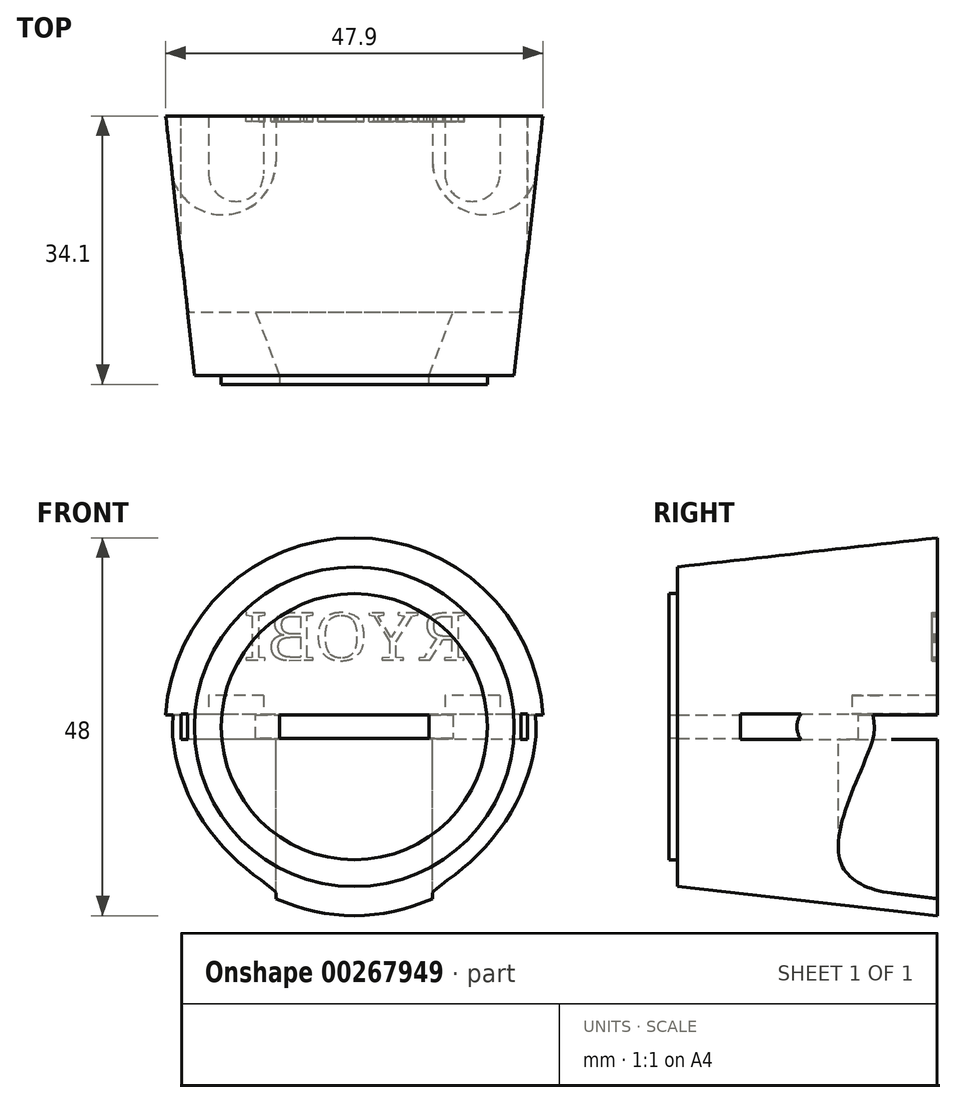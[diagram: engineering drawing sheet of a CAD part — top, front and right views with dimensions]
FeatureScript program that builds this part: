
annotation { "Feature Type Name" : "Feature", "Feature Type Description" : "" }
export const myFeature = defineFeature(function(context is Context, id is Id, definition is map)
    precondition{}
    {
        {
            var Q0;
            Q0=qCreatedBy(makeId("Top.planeOp"),FACE);
            var sketch = newSketch(context, id + "F0", { "sketchPlane" : qUnion([Q0])});
            skLineSegment(sketch, "E0", {"start": v(-68.5, 0) * mm, "end": v(-16.9, 0) * mm, "construction": true});
            skLineSegment(sketch, "E1", {"start": v(0, 74.1) * mm, "end": v(0, -57) * mm, "construction": true});
            skLineSegment(sketch, "E2", {"start": v(-16.9, 0) * mm, "end": v(-20.3, 0) * mm});
            skLineSegment(sketch, "E3", {"start": v(-20.3, 0) * mm, "end": v(-24, 33) * mm});
            skLineSegment(sketch, "E4", {"start": v(-24, 33) * mm, "end": v(0, 33) * mm});
            skLineSegment(sketch, "E5", {"start": v(0, 33) * mm, "end": v(0, 0) * mm});
            skLineSegment(sketch, "E6", {"start": v(-16.9, 0) * mm, "end": v(-16.9, -1.1) * mm});
            skLineSegment(sketch, "E7", {"start": v(-16.9, -1.1) * mm, "end": v(0, -1.1) * mm});
            skLineSegment(sketch, "E8.trimOffspring", {"start": v(0, 0) * mm, "end": v(74.38, 0) * mm, "construction": true});
            skLineSegment(sketch, "E9", {"start": v(0, -1.1) * mm, "end": v(0, 0) * mm});
            skSolve(sketch);
        }
        {
            var Q0;
            Q0=makeQuery(id+"F0.imprint","IMPRINT",FACE,{"disambiguationData":[TD([[makeQuery(id+"F0.imprint","IMPRINT",EDGE,{"derivedFrom":sQuery(id+"F0.wireOp",EDGE,"E2")}),-1.0]])]});
            var Q1;
            Q1=sQuery(id+"F0.wireOp",EDGE,"E1");
            revolve(context, id + "F1", {"entities" : qUnion([Q0]), "axis" : qUnion([Q1]), "revolveType" : RevolveType.FULL});
        }
        {
            var Q0;
            Q0=makeQuery(id+"F1.opRevolve","SWEPT_FACE",FACE,{"disambiguationData":[OSD([sQuery(id+"F0.wireOp",EDGE,"E4")])]});
            var sketch = newSketch(context, id + "F2", { "sketchPlane" : qUnion([Q0])});
            skLineSegment(sketch, "E10", {"start": v(-37.33, 0) * mm, "end": v(38.29, 0) * mm, "construction": true});
            skLineSegment(sketch, "E11", {"start": v(0, 36.13) * mm, "end": v(0, -36.43) * mm, "construction": true});
            skLineSegment(sketch, "E12", {"start": v(-22, 0) * mm, "end": v(-22, 1.6) * mm});
            skLineSegment(sketch, "E13", {"start": v(-22, 1.6) * mm, "end": v(0, 1.6) * mm});
            skLineSegment(sketch, "E14.MirrorCS", {"start": v(-22, -1.6) * mm, "end": v(0, -1.6) * mm});
            skLineSegment(sketch, "E15.MirrorCS", {"start": v(-22, 0) * mm, "end": v(-22, -1.6) * mm});
            skLineSegment(sketch, "E16.MirrorCS", {"start": v(22, 1.6) * mm, "end": v(0, 1.6) * mm});
            skLineSegment(sketch, "E17.MirrorCS", {"start": v(22, -1.6) * mm, "end": v(0, -1.6) * mm});
            skLineSegment(sketch, "E18.MirrorCS", {"start": v(22, 0) * mm, "end": v(22, 1.6) * mm});
            skLineSegment(sketch, "E19.MirrorCS", {"start": v(22, 0) * mm, "end": v(22, -1.6) * mm});
            skSolve(sketch);
        }
        {
            var Q0;
            Q0=qCreatedBy(makeId("Top.planeOp"),FACE);
            var sketch = newSketch(context, id + "F3", { "sketchPlane" : qUnion([Q0])});
            skLineSegment(sketch, "E20", {"start": v(22, 33.22) * mm, "end": v(-22, 33.22) * mm});
            skLineSegment(sketch, "E21", {"start": v(-22, 33.22) * mm, "end": v(-9.5, 0) * mm});
            skLineSegment(sketch, "E22", {"start": v(9.5, 0) * mm, "end": v(22, 33.22) * mm});
            skLineSegment(sketch, "E23", {"start": v(-9.5, 0) * mm, "end": v(-9.5, -1.28) * mm});
            skLineSegment(sketch, "E24", {"start": v(9.5, -1.28) * mm, "end": v(9.5, 0) * mm});
            skLineSegment(sketch, "E25", {"start": v(-9.5, -1.28) * mm, "end": v(9.5, -1.28) * mm});
            skLineSegment(sketch, "E26", {"start": v(-23.43, 20.06) * mm, "end": v(-23.43, 27.36) * mm, "construction": true});
            skLineSegment(sketch, "E27", {"start": v(23.97, 20.01) * mm, "end": v(23.97, 26.32) * mm, "construction": true});
            skLineSegment(sketch, "E28", {"start": v(-32.98, 14.8) * mm, "end": v(30.34, 14.8) * mm, "construction": true});
            skSolve(sketch);
        }
        {
            var Q0;
            Q0 = qSketchRegion(id + "F3", true);
            extrude(context, id + "F4", {"entities" : qUnion([Q0]), "operationType" : NewBodyOperationType.REMOVE, "endBound" : BoundingType.SYMMETRIC, "depth" : 3 * mm, "offsetDistance" : 25 * mm});
        }
        {
            var Q0;
            Q0=qCreatedBy(makeId("Top.planeOp"),FACE);
            var sketch = newSketch(context, id + "F5", { "sketchPlane" : qUnion([Q0])});
            skLineSegment(sketch, "E29", {"start": v(-24.03, 33) * mm, "end": v(-9.95, 33) * mm});
            skLineSegment(sketch, "E30", {"start": v(-9.95, 33) * mm, "end": v(-9.95, 27.19) * mm});
            skLineSegment(sketch, "E31", {"start": v(-24.03, 33) * mm, "end": v(-23.46, 27.19) * mm});
            skArc(sketch, "E32", {"start": v(-23.46, 27.19) * mm, "mid": v(-16.7, 20.43) * mm, "end": v(-9.95, 27.19) * mm});
            skLineSegment(sketch, "E33", {"start": v(0, 25.07) * mm, "end": v(0, -8.05) * mm, "construction": true});
            skLineSegment(sketch, "E34.MirrorCS", {"start": v(9.95, 33) * mm, "end": v(9.95, 27.19) * mm});
            skArc(sketch, "E35.MirrorCS", {"start": v(23.46, 27.19) * mm, "mid": v(16.7, 20.43) * mm, "end": v(9.95, 27.19) * mm});
            skLineSegment(sketch, "E36.MirrorCS", {"start": v(24.03, 33) * mm, "end": v(23.46, 27.19) * mm});
            skLineSegment(sketch, "E37.MirrorCS", {"start": v(24.03, 33) * mm, "end": v(9.95, 33) * mm});
            skSolve(sketch);
        }
        {
            var Q0;
            Q0 = qSketchRegion(id + "F5", true);
            extrude(context, id + "F6", {"entities" : qUnion([Q0]), "operationType" : NewBodyOperationType.REMOVE, "oppositeDirection" : true, "depth" : 25 * mm});
        }
        {
            var Q0;
            Q0 = qSketchRegion(id + "F5", true);
            extrude(context, id + "F7", {"entities" : qUnion([Q0]), "operationType" : NewBodyOperationType.REMOVE, "endBound" : BoundingType.SYMMETRIC, "oppositeDirection" : true, "depth" : 3 * mm});
        }
        {
            var Q0;
            Q0=makeQuery(id+"F7.boolean.opBoolean","MERGE",FACE,{"derivedFrom":[makeQuery(id+"F4.boolean.opBoolean","COPY",FACE,{"derivedFrom":makeQuery(id+"F4.opExtrude","CAP_FACE",FACE,{"disambiguationData":[OSD([sQuery(id+"F3.wireOp",EDGE,"E20"),sQuery(id+"F3.wireOp",EDGE,"E21"),sQuery(id+"F3.wireOp",EDGE,"E22"),sQuery(id+"F3.wireOp",EDGE,"E23"),sQuery(id+"F3.wireOp",EDGE,"E24"),sQuery(id+"F3.wireOp",EDGE,"E25")])],"isStart":false})}),makeQuery(id+"F7.opExtrude","CAP_FACE",FACE,{"disambiguationData":[OSD([sQuery(id+"F5.wireOp",EDGE,"E29"),sQuery(id+"F5.wireOp",EDGE,"E30"),sQuery(id+"F5.wireOp",EDGE,"E31"),sQuery(id+"F5.wireOp",EDGE,"E32")])],"isStart":true}),makeQuery(id+"F7.opExtrude","CAP_FACE",FACE,{"disambiguationData":[OSD([sQuery(id+"F5.wireOp",EDGE,"E34.MirrorCS"),sQuery(id+"F5.wireOp",EDGE,"E35.MirrorCS"),sQuery(id+"F5.wireOp",EDGE,"E36.MirrorCS"),sQuery(id+"F5.wireOp",EDGE,"E37.MirrorCS")])],"isStart":true})]});
            cPlane(context, id + "F8", {"entities" : qUnion([Q0]), "cplaneType" : CPlaneType.OFFSET, "offset" : 0 * mm, "width" : 150 * mm, "height" : 150 * mm});
        }
        {
            var Q0;
            Q0=qCreatedBy(id+"F8.planeOp",FACE);
            var sketch = newSketch(context, id + "F9", { "sketchPlane" : qUnion([Q0])});
            skLineSegment(sketch, "E38", {"start": v(0, -25.68) * mm, "end": v(0, 5.25) * mm, "construction": true});
            skLineSegment(sketch, "E39", {"start": v(15, -21.72) * mm, "end": v(15, 4.4) * mm, "construction": true});
            skLineSegment(sketch, "E40", {"start": v(-15, -24.72) * mm, "end": v(-15, 5.76) * mm, "construction": true});
            skLineSegment(sketch, "E41", {"start": v(25.34, -20) * mm, "end": v(-31.24, -20) * mm, "construction": true});
            skLineSegment(sketch, "E42", {"start": v(26.27, -11) * mm, "end": v(-28.57, -11) * mm, "construction": true});
            skLineSegment(sketch, "E43", {"start": v(18.5, -33) * mm, "end": v(18.5, -25.64) * mm});
            skLineSegment(sketch, "E44.MirrorCS", {"start": v(11.5, -33) * mm, "end": v(11.5, -25.64) * mm});
            skLineSegment(sketch, "E45.MirrorCS", {"start": v(-18.5, -33) * mm, "end": v(-18.5, -25.64) * mm});
            skLineSegment(sketch, "E46.MirrorCS", {"start": v(-11.5, -33) * mm, "end": v(-11.5, -25.64) * mm});
            skPoint(sketch, "E47.trimOffspring.end.orphan", {"position": v(18.5, -9.32) * mm});
            skPoint(sketch, "E48.trimOffspring.end.orphan", {"position": v(11.5, -9.32) * mm});
            skPoint(sketch, "E49.trimOffspring.end.orphan", {"position": v(-11.5, -9.32) * mm});
            skPoint(sketch, "E50.trimOffspring.end.orphan", {"position": v(-18.5, -9.32) * mm});
            skLineSegment(sketch, "E51", {"start": v(18.5, -33) * mm, "end": v(11.5, -33) * mm});
            skLineSegment(sketch, "E52", {"start": v(-11.5, -33) * mm, "end": v(-18.5, -33) * mm});
            skArc(sketch, "E53", {"start": v(-11.5, -25.64) * mm, "mid": v(-15, -22.14) * mm, "end": v(-18.5, -25.64) * mm});
            skArc(sketch, "E54.MirrorCS", {"start": v(11.5, -25.64) * mm, "mid": v(15, -22.14) * mm, "end": v(18.5, -25.64) * mm});
            skSolve(sketch);
        }
        {
            var Q0;
            Q0 = qSketchRegion(id + "F9", true);
            extrude(context, id + "F10", {"entities" : qUnion([Q0]), "operationType" : NewBodyOperationType.REMOVE, "oppositeDirection" : true, "depth" : 2.5 * mm});
        }
        {
            var Q0;
            Q0=makeQuery(id+"F2.imprint","IMPRINT",FACE,{"disambiguationData":[TD([[makeQuery(id+"F2.imprint","IMPRINT",EDGE,{"derivedFrom":sQuery(id+"F2.wireOp",EDGE,"E12")}),1.0]])]});
            cPlane(context, id + "F11", {"entities" : qUnion([Q0]), "cplaneType" : CPlaneType.OFFSET, "offset" : 0 * mm, "width" : 150 * mm, "height" : 150 * mm});
        }
        {
            var Q0;
            Q0=qCreatedBy(id+"F11.planeOp",FACE);
            var sketch = newSketch(context, id + "F12", { "sketchPlane" : qUnion([Q0])});
            skText(sketch, "E55", { "text": "RYOBI", "fontName": "Tinos-Regular.ttf"});
            const initialGuessF12  = {"E55": [-0.01425, 0.00847, 1, 0, 0.00655]};
            skSetInitialGuess(sketch, initialGuessF12);
            skSolve(sketch);
        }
        {
            var Q0;
            Q0 = qSketchRegion(id + "F12", true);
            extrude(context, id + "F13", {"entities" : qUnion([Q0]), "operationType" : NewBodyOperationType.REMOVE, "oppositeDirection" : true, "depth" : .7 * mm, "offsetDistance" : 25 * mm});
        }
        {
            var Q0;
            Q0 = qSketchRegion(id + "F2", true);
            extrude(context, id + "F14", {"entities" : qUnion([Q0]), "operationType" : NewBodyOperationType.REMOVE, "oppositeDirection" : true, "depth" : 25 * mm});
        }
    });
